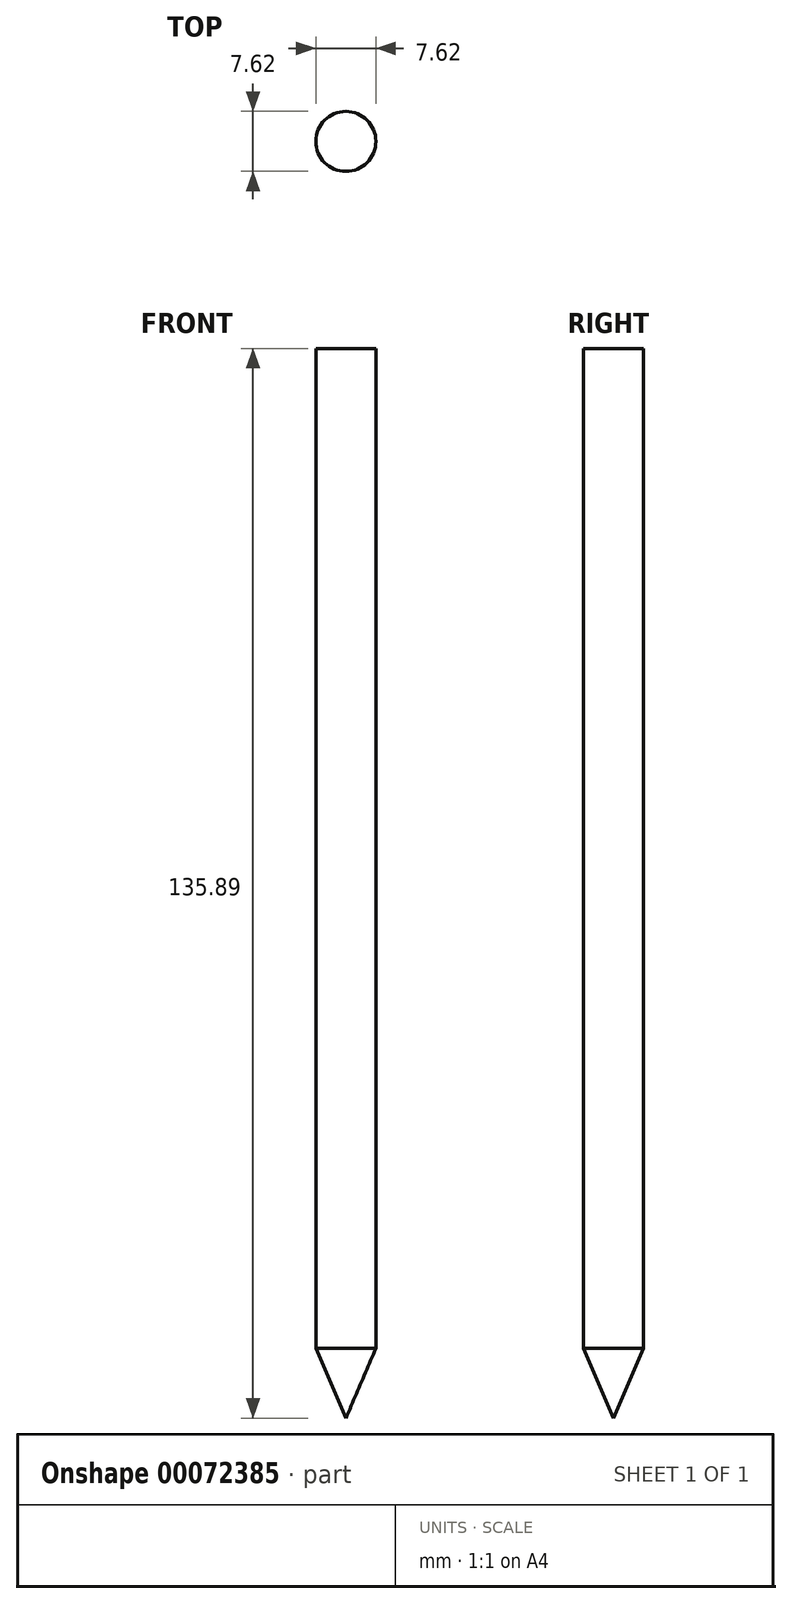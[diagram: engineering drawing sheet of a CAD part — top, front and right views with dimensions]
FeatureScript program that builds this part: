
annotation { "Feature Type Name" : "Feature", "Feature Type Description" : "" }
export const myFeature = defineFeature(function(context is Context, id is Id, definition is map)
    precondition{}
    {
        {
            var Q0;
            Q0=qCreatedBy(makeId("Top.planeOp"),FACE);
            var sketch = newSketch(context, id + "F0", { "sketchPlane" : qUnion([Q0])});
            skCircle(sketch, "E0", {"center": v(0, 0) * mm, "radius": 3.81 * mm});
            skSolve(sketch);
        }
        {
            var Q0;
            Q0 = qSketchRegion(id + "F0", true);
            extrude(context, id + "F1", {"entities" : qUnion([Q0]), "depth" : 127 * mm});
        }
        {
            var Q0;
            Q0=qCreatedBy(makeId("Front.planeOp"),FACE);
            var sketch = newSketch(context, id + "F2", { "sketchPlane" : qUnion([Q0])});
            skLineSegment(sketch, "E1", {"start": v(0, 0) * mm, "end": v(0, -8.9) * mm});
            skLineSegment(sketch, "E2", {"start": v(0, -8.9) * mm, "end": v(3.81, 0) * mm});
            skLineSegment(sketch, "E3", {"start": v(3.81, 0) * mm, "end": v(0, 0) * mm});
            skSolve(sketch);
        }
        {
            var Q0;
            Q0=makeQuery(id+"F2.imprint","IMPRINT",FACE,{"disambiguationData":[TD([[makeQuery(id+"F2.imprint","IMPRINT",EDGE,{"derivedFrom":sQuery(id+"F2.wireOp",EDGE,"E1")}),1.0]])]});
            var Q1;
            Q1=sQuery(id+"F2.wireOp",EDGE,"E1");
            revolve(context, id + "F3", {"operationType" : NewBodyOperationType.ADD, "entities" : qUnion([Q0]), "axis" : qUnion([Q1]), "revolveType" : RevolveType.FULL});
        }
    });
